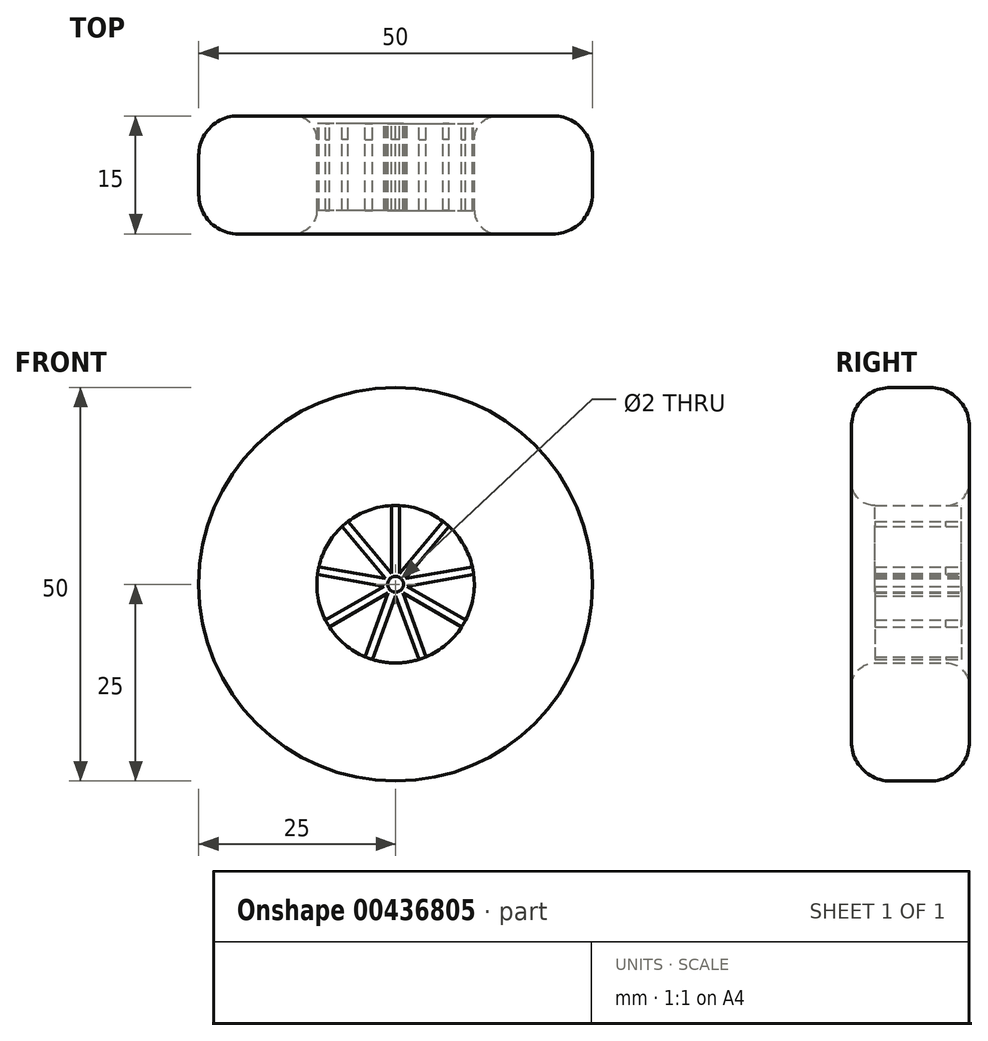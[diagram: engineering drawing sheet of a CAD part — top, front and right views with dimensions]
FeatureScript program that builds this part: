
annotation { "Feature Type Name" : "Feature", "Feature Type Description" : "" }
export const myFeature = defineFeature(function(context is Context, id is Id, definition is map)
    precondition{}
    {
        {
            var Q0;
            Q0=qCreatedBy(makeId("Front.planeOp"),FACE);
            var sketch = newSketch(context, id + "F0", { "sketchPlane" : qUnion([Q0])});
            skCircle(sketch, "E0", {"center": v(0, 0) * mm, "radius": 25 * mm});
            skCircle(sketch, "E1", {"center": v(0, 0) * mm, "radius": 10 * mm});
            skSolve(sketch);
        }
        {
            var Q0;
            Q0=makeQuery(id+"F0.imprint","IMPRINT",FACE,{"disambiguationData":[TD([[makeQuery(id+"F0.imprint","IMPRINT",EDGE,{"derivedFrom":sQuery(id+"F0.wireOp",EDGE,"E0")}),1.0]])]});
            extrude(context, id + "F1", {"entities" : qUnion([Q0]), "depth" : 15 * mm});
        }
        {
            var Q0;
            Q0=makeQuery(id+"F1.opExtrude","CAP_EDGE",EDGE,{"disambiguationData":[OSD([sQuery(id+"F0.wireOp",EDGE,"E0")])],"isStart":false});
            fillet(context, id + "F2", {"entities" : qUnion([Q0]), "radius" : 5 * mm, "tangentPropagation" : true, "allowEdgeOverflow" : false});
        }
        {
            var Q0;
            Q0=makeQuery(id+"F1.opExtrude","CAP_EDGE",EDGE,{"disambiguationData":[OSD([sQuery(id+"F0.wireOp",EDGE,"E1")])],"isStart":false});
            fillet(context, id + "F3", {"entities" : qUnion([Q0]), "radius" : 3 * mm, "tangentPropagation" : true, "allowEdgeOverflow" : false});
        }
        {
            var Q0;
            Q0=makeQuery(id+"F1.opExtrude","CAP_EDGE",EDGE,{"disambiguationData":[OSD([sQuery(id+"F0.wireOp",EDGE,"E0")])],"isStart":true});
            fillet(context, id + "F4", {"entities" : qUnion([Q0]), "radius" : 5 * mm, "tangentPropagation" : true, "allowEdgeOverflow" : false});
        }
        {
            var Q0;
            Q0=makeQuery(id+"F1.opExtrude","CAP_EDGE",EDGE,{"disambiguationData":[OSD([sQuery(id+"F0.wireOp",EDGE,"E1")])],"isStart":true});
            fillet(context, id + "F5", {"entities" : qUnion([Q0]), "radius" : 3 * mm, "tangentPropagation" : true, "allowEdgeOverflow" : false});
        }
        {
            var Q0;
            Q0=qCreatedBy(makeId("Front.planeOp"),FACE);
            var sketch = newSketch(context, id + "F6", { "sketchPlane" : qUnion([Q0])});
            skLineSegment(sketch, "E2.trimOffspring", {"start": v(-0.5, 1.37) * mm, "end": v(-0.5, 9.99) * mm});
            skLineSegment(sketch, "E3.trimOffspring", {"start": v(-0.5, 1.37) * mm, "end": v(-6.04, 7.97) * mm});
            skLineSegment(sketch, "E4.trimOffspring", {"start": v(-0.94, -1.12) * mm, "end": v(-8.4, -5.43) * mm});
            skLineSegment(sketch, "E5.trimOffspring", {"start": v(-0.94, -1.12) * mm, "end": v(-3.89, -9.21) * mm});
            skLineSegment(sketch, "E6.trimOffspring", {"start": v(-1.44, -0.25) * mm, "end": v(-9.92, 1.24) * mm});
            skLineSegment(sketch, "E7.trimOffspring", {"start": v(-1.44, -0.25) * mm, "end": v(-8.9, -4.56) * mm});
            skLineSegment(sketch, "E8.trimOffspring", {"start": v(-1.27, 0.73) * mm, "end": v(-6.8, 7.33) * mm});
            skLineSegment(sketch, "E9.trimOffspring", {"start": v(-1.27, 0.73) * mm, "end": v(-9.75, 2.23) * mm});
            skLineSegment(sketch, "E10.trimOffspring", {"start": v(1.27, 0.73) * mm, "end": v(9.75, 2.23) * mm});
            skLineSegment(sketch, "E11.trimOffspring", {"start": v(1.27, 0.73) * mm, "end": v(6.8, 7.33) * mm});
            skLineSegment(sketch, "E12.trimOffspring", {"start": v(0.5, 1.37) * mm, "end": v(6.04, 7.97) * mm});
            skLineSegment(sketch, "E13.trimOffspring", {"start": v(0.94, -1.12) * mm, "end": v(3.89, -9.21) * mm});
            skLineSegment(sketch, "E14.trimOffspring", {"start": v(0.94, -1.12) * mm, "end": v(8.4, -5.43) * mm});
            skLineSegment(sketch, "E15.trimOffspring", {"start": v(0, -1.46) * mm, "end": v(-2.95, -9.56) * mm});
            skLineSegment(sketch, "E16.trimOffspring", {"start": v(0, -1.46) * mm, "end": v(2.95, -9.56) * mm});
            skLineSegment(sketch, "E17.trimOffspring", {"start": v(0.5, 1.37) * mm, "end": v(0.5, 9.99) * mm});
            skCircle(sketch, "E18", {"center": v(0, 0) * mm, "radius": 1 * mm});
            skLineSegment(sketch, "E19.0", {"start": v(1.44, -0.25) * mm, "end": v(9.92, 1.24) * mm});
            skLineSegment(sketch, "E20.0", {"start": v(1.44, -0.25) * mm, "end": v(8.9, -4.56) * mm});
            skArc(sketch, "E21", {"start": v(-6.04, 7.97) * mm, "mid": v(-6.43, 7.66) * mm, "end": v(-6.8, 7.33) * mm});
            skArc(sketch, "E22.trimOffspring", {"start": v(0.5, 9.99) * mm, "mid": v(0, 10) * mm, "end": v(-0.5, 9.99) * mm});
            skArc(sketch, "E23.trimOffspring", {"start": v(6.8, 7.33) * mm, "mid": v(6.43, 7.66) * mm, "end": v(6.04, 7.97) * mm});
            skArc(sketch, "E24.trimOffspring", {"start": v(9.92, 1.24) * mm, "mid": v(9.85, 1.74) * mm, "end": v(9.75, 2.23) * mm});
            skArc(sketch, "E25.trimOffspring", {"start": v(8.4, -5.43) * mm, "mid": v(8.66, -5) * mm, "end": v(8.9, -4.56) * mm});
            skArc(sketch, "E26.trimOffspring", {"start": v(2.95, -9.56) * mm, "mid": v(3.42, -9.4) * mm, "end": v(3.89, -9.21) * mm});
            skArc(sketch, "E27.trimOffspring", {"start": v(-3.89, -9.21) * mm, "mid": v(-3.42, -9.4) * mm, "end": v(-2.95, -9.56) * mm});
            skArc(sketch, "E28.trimOffspring", {"start": v(-8.9, -4.56) * mm, "mid": v(-8.66, -5) * mm, "end": v(-8.4, -5.43) * mm});
            skArc(sketch, "E29.trimOffspring", {"start": v(-9.75, 2.23) * mm, "mid": v(-9.85, 1.74) * mm, "end": v(-9.92, 1.24) * mm});
            skSolve(sketch);
        }
        {
            var Q0;
            Q0 = qSketchRegion(id + "F6", true);
            extrude(context, id + "F7", {"entities" : qUnion([Q0]), "operationType" : NewBodyOperationType.ADD, "depth" : 12 * mm});
        }
        {
            var Q0;
            Q0 = qSketchRegion(id + "F6", true);
            extrude(context, id + "F8", {"entities" : qUnion([Q0]), "operationType" : NewBodyOperationType.REMOVE, "depth" : 1 * mm});
        }
    });
